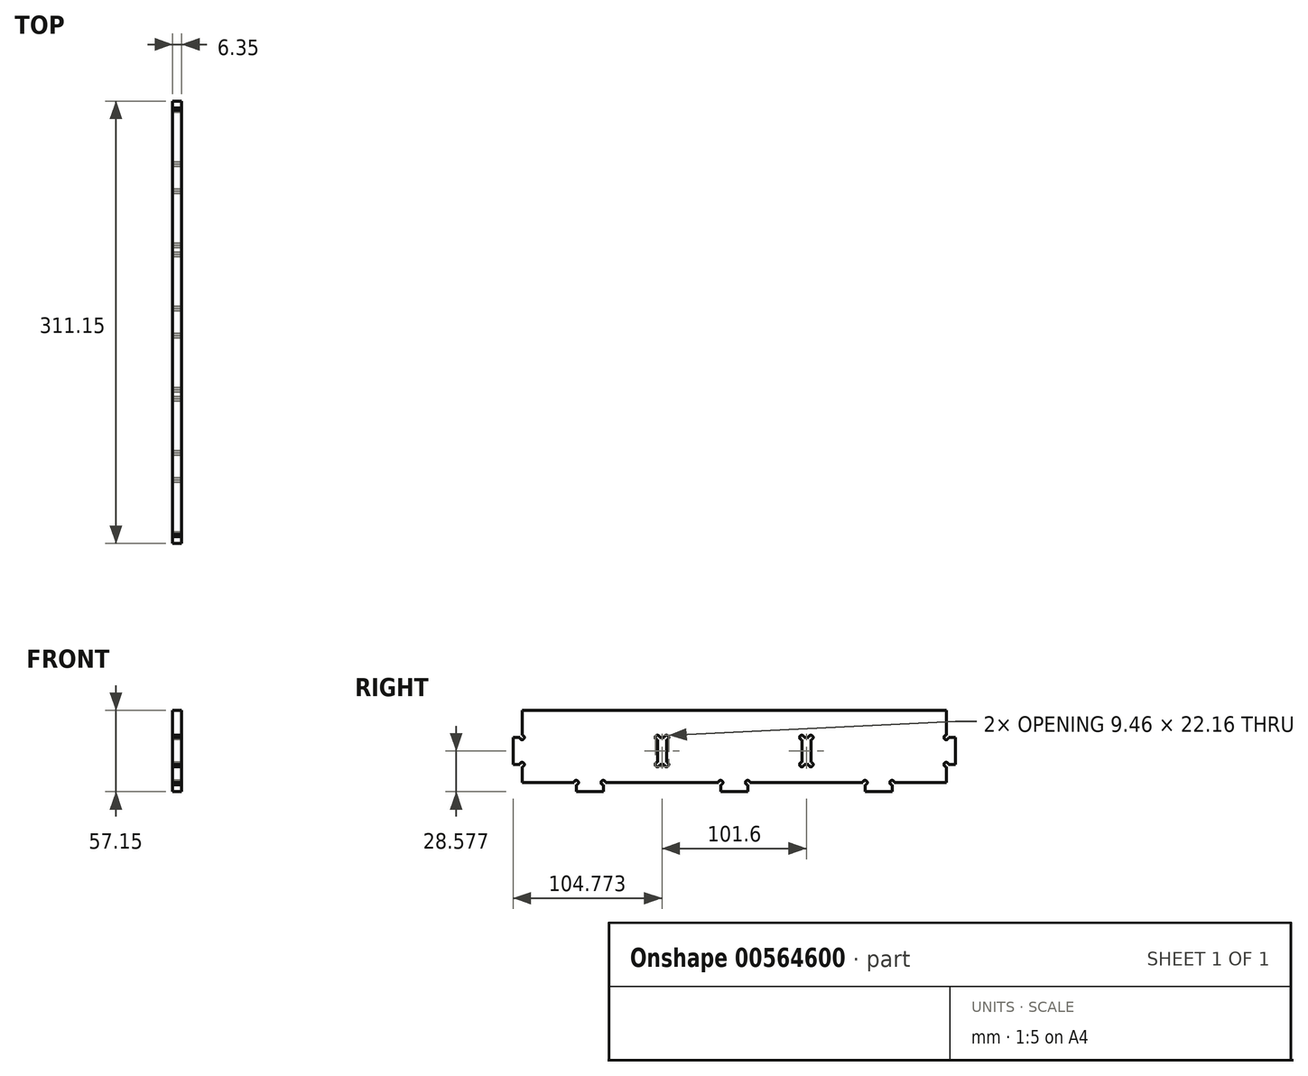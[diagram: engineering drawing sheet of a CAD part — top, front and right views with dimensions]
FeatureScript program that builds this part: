
annotation { "Feature Type Name" : "Feature", "Feature Type Description" : "" }
export const myFeature = defineFeature(function(context is Context, id is Id, definition is map)
    precondition{}
    {
        {
            var Q0;
            Q0=qCreatedBy(makeId("Right.planeOp"),FACE);
            var sketch = newSketch(context, id + "F0", { "sketchPlane" : qUnion([Q0])});
            skLineSegment(sketch, "E0.bottom", {"start": v(-141.97, 50.51) * mm, "end": v(156.48, 50.51) * mm});
            skLineSegment(sketch, "E0.top", {"start": v(-141.97, -0.29) * mm, "end": v(156.48, -0.29) * mm});
            skLineSegment(sketch, "E0.left", {"start": v(-141.97, 50.51) * mm, "end": v(-141.97, -0.29) * mm});
            skLineSegment(sketch, "E0.right", {"start": v(156.48, 50.51) * mm, "end": v(156.48, -0.29) * mm});
            skLineSegment(sketch, "E1.bottom", {"start": v(61.23, 31.46) * mm, "end": v(54.88, 31.46) * mm});
            skLineSegment(sketch, "E1.top", {"start": v(61.23, 12.41) * mm, "end": v(54.88, 12.41) * mm});
            skLineSegment(sketch, "E1.left", {"start": v(61.23, 31.46) * mm, "end": v(61.23, 12.41) * mm});
            skLineSegment(sketch, "E1.right", {"start": v(54.88, 31.46) * mm, "end": v(54.88, 12.41) * mm});
            skLineSegment(sketch, "E2.bottom", {"start": v(-40.37, 31.46) * mm, "end": v(-46.72, 31.46) * mm});
            skLineSegment(sketch, "E2.top", {"start": v(-40.37, 12.41) * mm, "end": v(-46.72, 12.41) * mm});
            skLineSegment(sketch, "E2.left", {"start": v(-40.37, 31.46) * mm, "end": v(-40.37, 12.41) * mm});
            skLineSegment(sketch, "E2.right", {"start": v(-46.72, 31.46) * mm, "end": v(-46.72, 12.41) * mm});
            skLineSegment(sketch, "E3.bottom", {"start": v(-141.97, 31.46) * mm, "end": v(-148.32, 31.46) * mm});
            skLineSegment(sketch, "E3.top", {"start": v(-141.97, 12.41) * mm, "end": v(-148.32, 12.41) * mm});
            skLineSegment(sketch, "E3.left", {"start": v(-141.97, 31.46) * mm, "end": v(-141.97, 12.41) * mm});
            skLineSegment(sketch, "E3.right", {"start": v(-148.32, 31.46) * mm, "end": v(-148.32, 12.41) * mm});
            skLineSegment(sketch, "E4.bottom", {"start": v(156.48, 31.46) * mm, "end": v(162.83, 31.46) * mm});
            skLineSegment(sketch, "E4.top", {"start": v(156.48, 12.41) * mm, "end": v(162.83, 12.41) * mm});
            skLineSegment(sketch, "E4.left", {"start": v(156.48, 31.46) * mm, "end": v(156.48, 12.41) * mm});
            skLineSegment(sketch, "E4.right", {"start": v(162.83, 31.46) * mm, "end": v(162.83, 12.41) * mm});
            skLineSegment(sketch, "E5.bottom", {"start": v(-103.87, -0.29) * mm, "end": v(-84.82, -0.29) * mm});
            skLineSegment(sketch, "E5.top", {"start": v(-103.87, -6.64) * mm, "end": v(-84.82, -6.64) * mm});
            skLineSegment(sketch, "E5.left", {"start": v(-103.87, -0.29) * mm, "end": v(-103.87, -6.64) * mm});
            skLineSegment(sketch, "E5.right", {"start": v(-84.82, -0.29) * mm, "end": v(-84.82, -6.64) * mm});
            skLineSegment(sketch, "E6.bottom", {"start": v(-2.27, -0.29) * mm, "end": v(16.78, -0.29) * mm});
            skLineSegment(sketch, "E6.top", {"start": v(-2.27, -6.64) * mm, "end": v(16.78, -6.64) * mm});
            skLineSegment(sketch, "E6.left", {"start": v(-2.27, -0.29) * mm, "end": v(-2.27, -6.64) * mm});
            skLineSegment(sketch, "E6.right", {"start": v(16.78, -0.29) * mm, "end": v(16.78, -6.64) * mm});
            skLineSegment(sketch, "E7.bottom", {"start": v(99.33, -0.29) * mm, "end": v(118.38, -0.29) * mm});
            skLineSegment(sketch, "E7.top", {"start": v(99.33, -6.64) * mm, "end": v(118.38, -6.64) * mm});
            skLineSegment(sketch, "E7.left", {"start": v(99.33, -0.29) * mm, "end": v(99.33, -6.64) * mm});
            skLineSegment(sketch, "E7.right", {"start": v(118.38, -0.29) * mm, "end": v(118.38, -6.64) * mm});
            skPoint(sketch, "E8.visualSharp", {"position": v(-148.32, 31.46) * mm});
            skLineSegment(sketch, "E8.filletArc", {"start": v(-148.32, 31.46) * mm, "end": v(-148.32, 31.46) * mm});
            skPoint(sketch, "E9.visualSharp", {"position": v(-148.32, 12.41) * mm});
            skLineSegment(sketch, "E9.filletArc", {"start": v(-148.32, 12.41) * mm, "end": v(-148.32, 12.41) * mm});
            skPoint(sketch, "E10.visualSharp", {"position": v(-103.87, -6.64) * mm});
            skLineSegment(sketch, "E10.filletArc", {"start": v(-103.87, -6.64) * mm, "end": v(-103.87, -6.64) * mm});
            skPoint(sketch, "E11.visualSharp", {"position": v(-84.82, -6.64) * mm});
            skLineSegment(sketch, "E11.filletArc", {"start": v(-84.82, -6.64) * mm, "end": v(-84.82, -6.64) * mm});
            skPoint(sketch, "E12.visualSharp", {"position": v(-46.72, 31.46) * mm});
            skLineSegment(sketch, "E12.filletArc", {"start": v(-46.72, 31.46) * mm, "end": v(-46.72, 31.46) * mm});
            skPoint(sketch, "E13.visualSharp", {"position": v(-40.37, 31.46) * mm});
            skLineSegment(sketch, "E13.filletArc", {"start": v(-40.37, 31.46) * mm, "end": v(-40.37, 31.46) * mm});
            skPoint(sketch, "E14.visualSharp", {"position": v(-40.37, 12.41) * mm});
            skLineSegment(sketch, "E14.filletArc", {"start": v(-40.37, 12.41) * mm, "end": v(-40.37, 12.41) * mm});
            skPoint(sketch, "E15.visualSharp", {"position": v(-46.72, 12.41) * mm});
            skLineSegment(sketch, "E15.filletArc", {"start": v(-46.72, 12.41) * mm, "end": v(-46.72, 12.41) * mm});
            skPoint(sketch, "E16.visualSharp", {"position": v(16.78, -6.64) * mm});
            skLineSegment(sketch, "E16.filletArc", {"start": v(16.78, -6.64) * mm, "end": v(16.78, -6.64) * mm});
            skPoint(sketch, "E17.visualSharp", {"position": v(-2.27, -6.64) * mm});
            skLineSegment(sketch, "E17.filletArc", {"start": v(-2.27, -6.64) * mm, "end": v(-2.27, -6.64) * mm});
            skPoint(sketch, "E18.visualSharp", {"position": v(61.23, 31.46) * mm});
            skLineSegment(sketch, "E18.filletArc", {"start": v(61.23, 31.46) * mm, "end": v(61.23, 31.46) * mm});
            skPoint(sketch, "E19.visualSharp", {"position": v(54.88, 31.46) * mm});
            skLineSegment(sketch, "E19.filletArc", {"start": v(54.88, 31.46) * mm, "end": v(54.88, 31.46) * mm});
            skPoint(sketch, "E20.visualSharp", {"position": v(61.23, 12.41) * mm});
            skLineSegment(sketch, "E20.filletArc", {"start": v(61.23, 12.41) * mm, "end": v(61.23, 12.41) * mm});
            skPoint(sketch, "E21.visualSharp", {"position": v(54.88, 12.41) * mm});
            skLineSegment(sketch, "E21.filletArc", {"start": v(54.88, 12.41) * mm, "end": v(54.88, 12.41) * mm});
            skPoint(sketch, "E22.visualSharp", {"position": v(99.33, -6.64) * mm});
            skLineSegment(sketch, "E22.filletArc", {"start": v(99.33, -6.64) * mm, "end": v(99.33, -6.64) * mm});
            skPoint(sketch, "E23.visualSharp", {"position": v(118.38, -6.64) * mm});
            skLineSegment(sketch, "E23.filletArc", {"start": v(118.38, -6.64) * mm, "end": v(118.38, -6.64) * mm});
            skPoint(sketch, "E24.visualSharp", {"position": v(162.83, 31.46) * mm});
            skLineSegment(sketch, "E24.filletArc", {"start": v(162.83, 31.46) * mm, "end": v(162.83, 31.46) * mm});
            skPoint(sketch, "E25.visualSharp", {"position": v(162.83, 12.41) * mm});
            skLineSegment(sketch, "E25.filletArc", {"start": v(162.83, 12.41) * mm, "end": v(162.83, 12.41) * mm});
            skCircle(sketch, "E26", {"center": v(-46.72, 31.46) * mm, "radius": 1.59 * mm});
            skCircle(sketch, "E27", {"center": v(-40.37, 31.46) * mm, "radius": 1.59 * mm});
            skCircle(sketch, "E28", {"center": v(-46.72, 12.41) * mm, "radius": 1.59 * mm});
            skCircle(sketch, "E29", {"center": v(-40.37, 12.41) * mm, "radius": 1.59 * mm});
            skCircle(sketch, "E30", {"center": v(-141.97, 31.46) * mm, "radius": 1.59 * mm});
            skCircle(sketch, "E31", {"center": v(-141.97, 12.41) * mm, "radius": 1.59 * mm});
            skCircle(sketch, "E32", {"center": v(-84.82, -0.29) * mm, "radius": 1.59 * mm});
            skCircle(sketch, "E33", {"center": v(-103.87, -0.29) * mm, "radius": 1.59 * mm});
            skCircle(sketch, "E34", {"center": v(-2.27, -0.29) * mm, "radius": 1.59 * mm});
            skCircle(sketch, "E35", {"center": v(16.78, -0.29) * mm, "radius": 1.59 * mm});
            skCircle(sketch, "E36", {"center": v(54.88, 31.46) * mm, "radius": 1.59 * mm});
            skCircle(sketch, "E37", {"center": v(61.23, 12.41) * mm, "radius": 1.59 * mm});
            skCircle(sketch, "E38", {"center": v(61.23, 31.46) * mm, "radius": 1.59 * mm});
            skCircle(sketch, "E39", {"center": v(54.88, 12.41) * mm, "radius": 1.59 * mm});
            skCircle(sketch, "E40", {"center": v(99.33, -0.29) * mm, "radius": 1.59 * mm});
            skCircle(sketch, "E41", {"center": v(118.38, -0.29) * mm, "radius": 1.59 * mm});
            skCircle(sketch, "E42", {"center": v(156.48, 31.46) * mm, "radius": 1.59 * mm});
            skCircle(sketch, "E43", {"center": v(156.48, 12.41) * mm, "radius": 1.59 * mm});
            skSolve(sketch);
        }
        {
            var Q0;
            {var subQ0=sQuery(id+"F0.wireOp",EDGE,"E3.right");Q0=makeQuery(id+"F0.imprint","IMPRINT",FACE,{"disambiguationData":[TD([[makeQuery(id+"F0.imprint","IMPRINT",EDGE,{"derivedFrom":subQ0}),1.0]])]});}
            var Q1;
            {var subQ58=sQuery(id+"F0.wireOp",EDGE,"E0.bottom");Q1=makeQuery(id+"F0.imprint","IMPRINT",FACE,{"disambiguationData":[TD([[makeQuery(id+"F0.imprint","IMPRINT",EDGE,{"derivedFrom":subQ58}),-1.0]])]});}
            var Q2;
            {var subQ1=sQuery(id+"F0.wireOp",EDGE,"E5.top");Q2=makeQuery(id+"F0.imprint","IMPRINT",FACE,{"disambiguationData":[TD([[makeQuery(id+"F0.imprint","IMPRINT",EDGE,{"derivedFrom":subQ1}),1.0]])]});}
            var Q3;
            {var subQ1=sQuery(id+"F0.wireOp",EDGE,"E6.top");Q3=makeQuery(id+"F0.imprint","IMPRINT",FACE,{"disambiguationData":[TD([[makeQuery(id+"F0.imprint","IMPRINT",EDGE,{"derivedFrom":subQ1}),1.0]])]});}
            var Q4;
            {var subQ1=sQuery(id+"F0.wireOp",EDGE,"E7.top");Q4=makeQuery(id+"F0.imprint","IMPRINT",FACE,{"disambiguationData":[TD([[makeQuery(id+"F0.imprint","IMPRINT",EDGE,{"derivedFrom":subQ1}),1.0]])]});}
            var Q5;
            {var subQ0=sQuery(id+"F0.wireOp",EDGE,"E4.right");Q5=makeQuery(id+"F0.imprint","IMPRINT",FACE,{"disambiguationData":[TD([[makeQuery(id+"F0.imprint","IMPRINT",EDGE,{"derivedFrom":subQ0}),-1.0]])]});}
            extrude(context, id + "F1", {"entities" : qUnion([Q0, Q1, Q2, Q3, Q4, Q5]), "depth" : 6.35 * mm, "offsetDistance" : 25.4 * mm});
        }
    });
